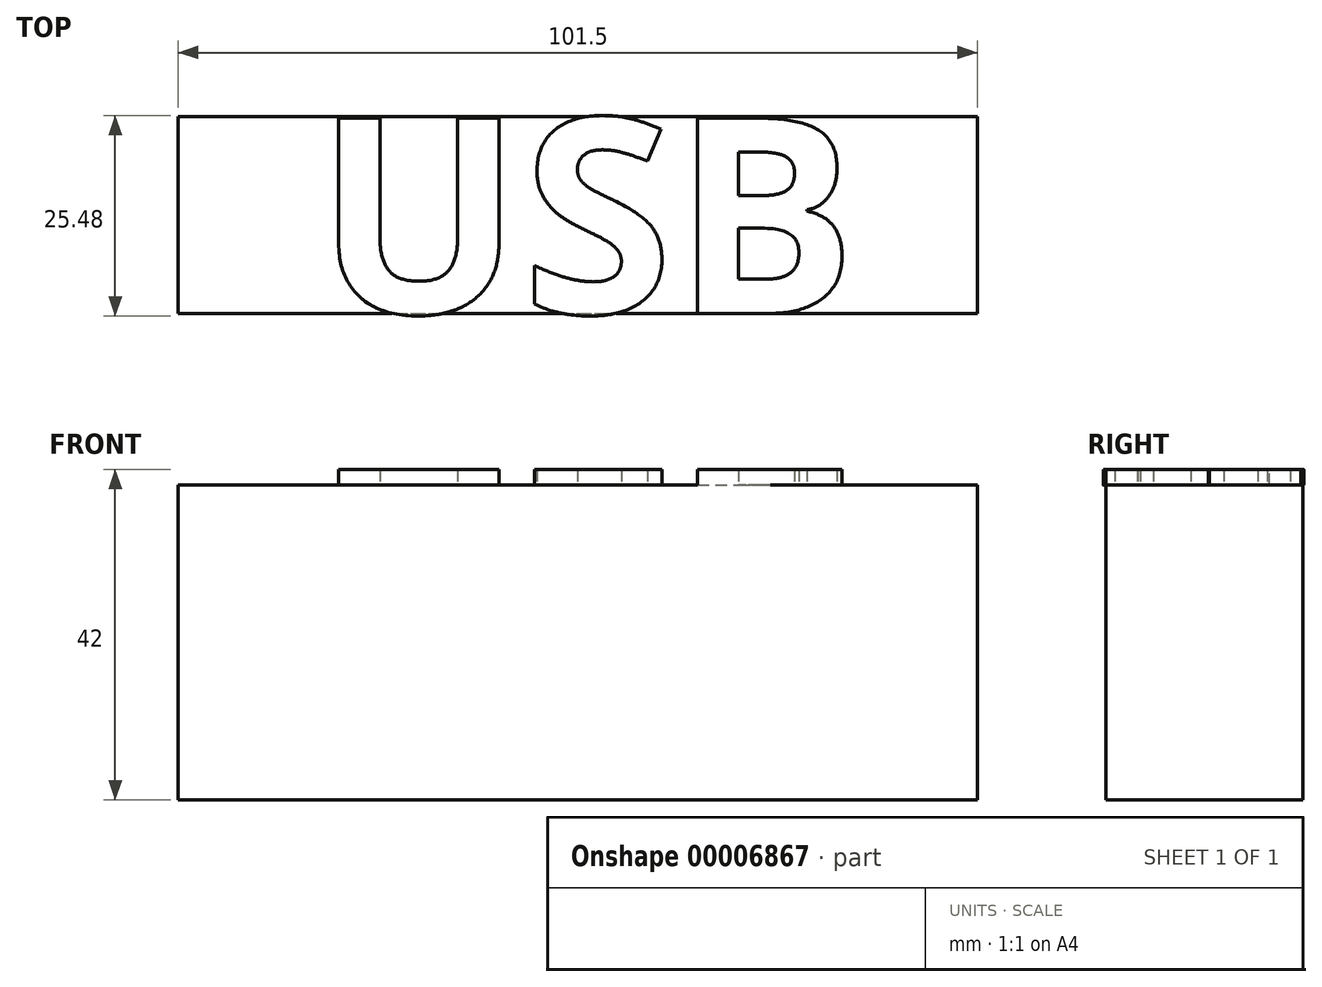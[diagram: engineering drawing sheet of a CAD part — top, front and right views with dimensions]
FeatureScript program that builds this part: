
annotation { "Feature Type Name" : "Feature", "Feature Type Description" : "" }
export const myFeature = defineFeature(function(context is Context, id is Id, definition is map)
    precondition{}
    {
        {
            var Q0;
            Q0=qCreatedBy(makeId("Top.planeOp"),FACE);
            var sketch = newSketch(context, id + "F0", { "sketchPlane" : qUnion([Q0])});
            skLineSegment(sketch, "E0.bottom", {"start": v(-23.08, 0) * mm, "end": v(78.42, 0) * mm});
            skLineSegment(sketch, "E0.top", {"start": v(-23.08, 25) * mm, "end": v(78.42, 25) * mm});
            skLineSegment(sketch, "E0.left", {"start": v(-23.08, 0) * mm, "end": v(-23.08, 25) * mm});
            skLineSegment(sketch, "E0.right", {"start": v(78.42, 0) * mm, "end": v(78.42, 25) * mm});
            skSolve(sketch);
        }
        {
            var Q0;
            Q0=makeQuery(id+"F0.imprint","IMPRINT",FACE,{"disambiguationData":[TD([[makeQuery(id+"F0.imprint","IMPRINT",EDGE,{"derivedFrom":sQuery(id+"F0.wireOp",EDGE,"E0.bottom")}),1.0]])]});
            extrude(context, id + "F1", {"entities" : qUnion([Q0]), "depth" : 40 * mm});
        }
        {
            var Q0;
            Q0=makeQuery(id+"F1.opExtrude","CAP_FACE",FACE,{"disambiguationData":[OSD([sQuery(id+"F0.wireOp",EDGE,"E0.bottom"),sQuery(id+"F0.wireOp",EDGE,"E0.top"),sQuery(id+"F0.wireOp",EDGE,"E0.left"),sQuery(id+"F0.wireOp",EDGE,"E0.right")])],"isStart":false});
            var sketch = newSketch(context, id + "F2", { "sketchPlane" : qUnion([Q0])});
            skText(sketch, "E1", { "text": "USB", "fontName": "OpenSans-Bold.ttf"});
            const initialGuessF2  = {"E1": [-0.00565, 0, 1, 0, 0.025]};
            skSetInitialGuess(sketch, initialGuessF2);
            skSolve(sketch);
        }
        {
            var Q0;
            Q0 = qSketchRegion(id + "F2", true);
            extrude(context, id + "F3", {"entities" : qUnion([Q0]), "operationType" : NewBodyOperationType.ADD, "depth" : 2 * mm});
        }
    });
